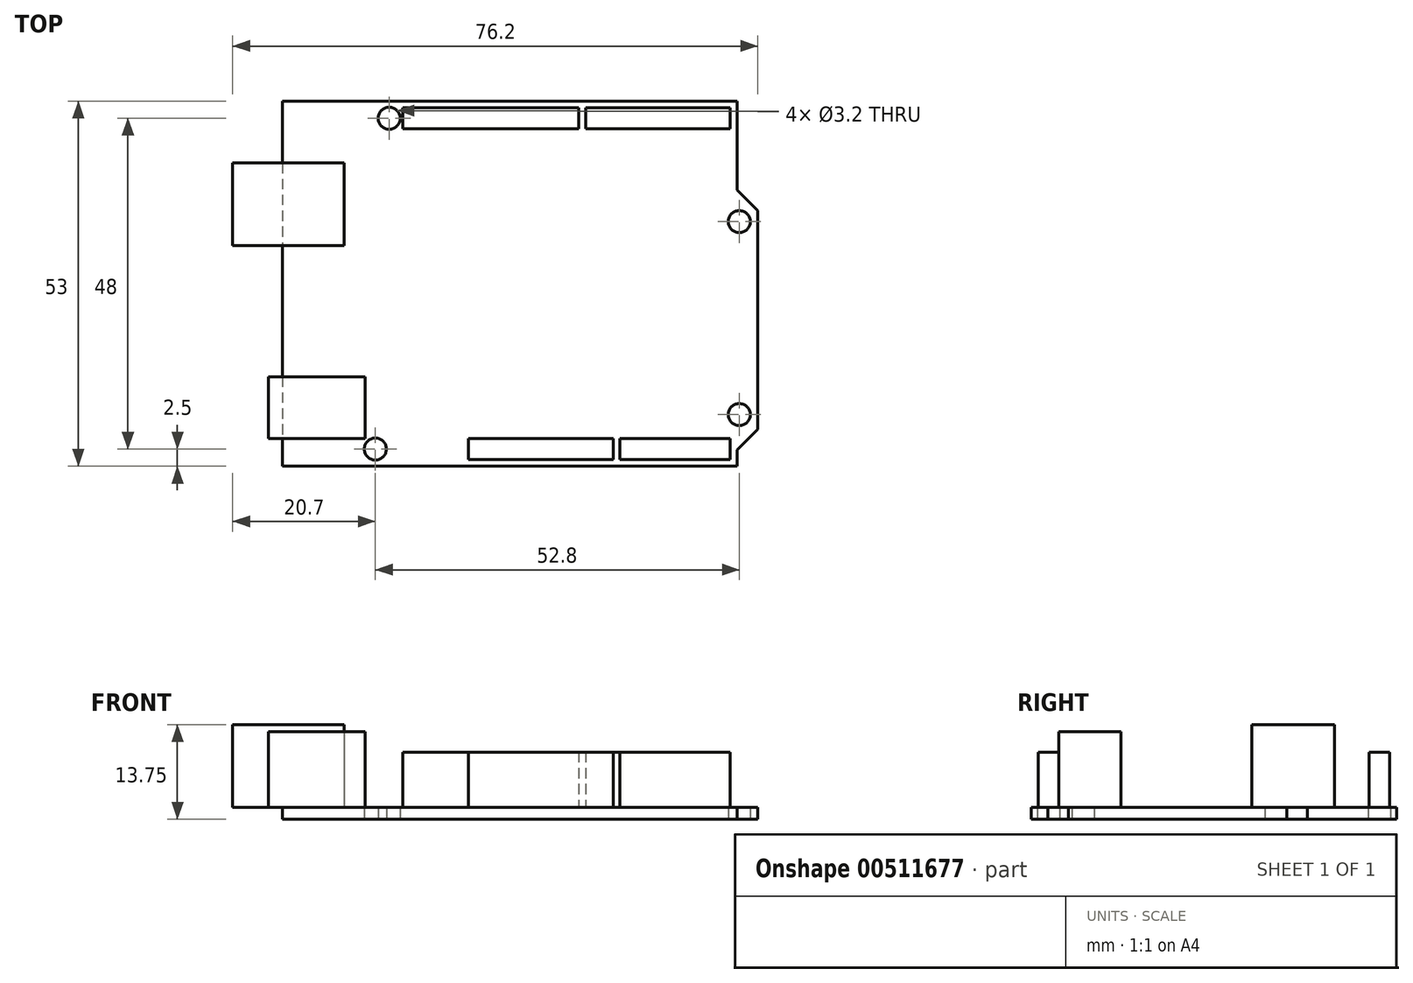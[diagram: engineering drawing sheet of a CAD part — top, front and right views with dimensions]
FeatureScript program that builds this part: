
annotation { "Feature Type Name" : "Feature", "Feature Type Description" : "" }
export const myFeature = defineFeature(function(context is Context, id is Id, definition is map)
    precondition{}
    {
        {
            var Q0;
            Q0=qCreatedBy(makeId("Top.planeOp"),FACE);
            var sketch = newSketch(context, id + "F0", { "sketchPlane" : qUnion([Q0])});
            skLineSegment(sketch, "E0.bottom", {"start": v(-36.44, 36.99) * mm, "end": v(32.56, 36.99) * mm});
            skLineSegment(sketch, "E0.top", {"start": v(-36.44, -16.01) * mm, "end": v(32.56, -16.01) * mm});
            skLineSegment(sketch, "E0.left", {"start": v(-36.44, 36.99) * mm, "end": v(-36.44, -16.01) * mm});
            skLineSegment(sketch, "E0.right", {"start": v(32.56, 36.99) * mm, "end": v(32.56, -16.01) * mm});
            skCircle(sketch, "E1", {"center": v(-22.94, -13.51) * mm, "radius": 1.6 * mm});
            skCircle(sketch, "E2", {"center": v(-20.94, 34.49) * mm, "radius": 1.6 * mm});
            skCircle(sketch, "E3", {"center": v(29.86, 19.49) * mm, "radius": 1.6 * mm});
            skCircle(sketch, "E4", {"center": v(29.86, -8.51) * mm, "radius": 1.6 * mm});
            skLineSegment(sketch, "E5", {"start": v(29.56, -16.01) * mm, "end": v(29.56, -13.64) * mm});
            skLineSegment(sketch, "E6", {"start": v(29.56, -13.64) * mm, "end": v(32.56, -10.64) * mm});
            skLineSegment(sketch, "E7", {"start": v(29.56, 36.99) * mm, "end": v(29.56, 24.07) * mm});
            skLineSegment(sketch, "E8", {"start": v(29.56, 24.07) * mm, "end": v(32.56, 21.07) * mm});
            skSolve(sketch);
        }
        {
            var Q0;
            {var subQ1=sQuery(id+"F0.wireOp",EDGE,"E0.left");Q0=makeQuery(id+"F0.imprint","IMPRINT",FACE,{"disambiguationData":[TD([[makeQuery(id+"F0.imprint","IMPRINT",EDGE,{"derivedFrom":subQ1}),1.0]])]});}
            extrude(context, id + "F1", {"entities" : qUnion([Q0]), "depth" : 1.75 * mm});
        }
        {
            var Q0;
            Q0=makeQuery(id+"F1.opExtrude","CAP_FACE",FACE,{"disambiguationData":[OSD([sQuery(id+"F0.wireOp",EDGE,"E0.bottom"),sQuery(id+"F0.wireOp",EDGE,"E0.top"),sQuery(id+"F0.wireOp",EDGE,"E0.left"),sQuery(id+"F0.wireOp",EDGE,"E0.right"),sQuery(id+"F0.wireOp",EDGE,"E1"),sQuery(id+"F0.wireOp",EDGE,"E2"),sQuery(id+"F0.wireOp",EDGE,"E3"),sQuery(id+"F0.wireOp",EDGE,"E4"),sQuery(id+"F0.wireOp",EDGE,"E5"),sQuery(id+"F0.wireOp",EDGE,"E6"),sQuery(id+"F0.wireOp",EDGE,"E7"),sQuery(id+"F0.wireOp",EDGE,"E8")])],"isStart":false});
            var sketch = newSketch(context, id + "F2", { "sketchPlane" : qUnion([Q0])});
            skLineSegment(sketch, "E9.bottom", {"start": v(-43.64, 27.99) * mm, "end": v(-27.44, 27.99) * mm});
            skLineSegment(sketch, "E9.top", {"start": v(-43.64, 15.99) * mm, "end": v(-27.44, 15.99) * mm});
            skLineSegment(sketch, "E9.left", {"start": v(-43.64, 27.99) * mm, "end": v(-43.64, 15.99) * mm});
            skLineSegment(sketch, "E9.right", {"start": v(-27.44, 27.99) * mm, "end": v(-27.44, 15.99) * mm});
            skSolve(sketch);
        }
        {
            var Q0;
            {var subQ0=sQuery(id+"F2.wireOp",EDGE,"E9.left");Q0=makeQuery(id+"F2.imprint","IMPRINT",FACE,{"disambiguationData":[TD([[makeQuery(id+"F2.imprint","IMPRINT",EDGE,{"derivedFrom":subQ0}),1.0]])]});}
            var Q1;
            {var subQ0=sQuery(id+"F2.wireOp",EDGE,"E9.right");Q1=makeQuery(id+"F2.imprint","IMPRINT",FACE,{"disambiguationData":[TD([[makeQuery(id+"F2.imprint","IMPRINT",EDGE,{"derivedFrom":subQ0}),-1.0]])]});}
            extrude(context, id + "F3", {"entities" : qUnion([Q0, Q1]), "operationType" : NewBodyOperationType.ADD, "depth" : 12 * mm});
        }
        {
            var Q0;
            Q0=makeQuery(id+"F1.opExtrude","CAP_FACE",FACE,{"disambiguationData":[OSD([sQuery(id+"F0.wireOp",EDGE,"E0.bottom"),sQuery(id+"F0.wireOp",EDGE,"E0.top"),sQuery(id+"F0.wireOp",EDGE,"E0.left"),sQuery(id+"F0.wireOp",EDGE,"E0.right"),sQuery(id+"F0.wireOp",EDGE,"E1"),sQuery(id+"F0.wireOp",EDGE,"E2"),sQuery(id+"F0.wireOp",EDGE,"E3"),sQuery(id+"F0.wireOp",EDGE,"E4"),sQuery(id+"F0.wireOp",EDGE,"E5"),sQuery(id+"F0.wireOp",EDGE,"E6"),sQuery(id+"F0.wireOp",EDGE,"E7"),sQuery(id+"F0.wireOp",EDGE,"E8")])],"isStart":false});
            var sketch = newSketch(context, id + "F4", { "sketchPlane" : qUnion([Q0])});
            skLineSegment(sketch, "E10.bottom", {"start": v(-38.44, -3.01) * mm, "end": v(-24.44, -3.01) * mm});
            skLineSegment(sketch, "E10.top", {"start": v(-38.44, -12.01) * mm, "end": v(-24.44, -12.01) * mm});
            skLineSegment(sketch, "E10.left", {"start": v(-38.44, -3.01) * mm, "end": v(-38.44, -12.01) * mm});
            skLineSegment(sketch, "E10.right", {"start": v(-24.44, -3.01) * mm, "end": v(-24.44, -12.01) * mm});
            skSolve(sketch);
        }
        {
            var Q0;
            {var subQ0=sQuery(id+"F4.wireOp",EDGE,"E10.right");Q0=makeQuery(id+"F4.imprint","IMPRINT",FACE,{"disambiguationData":[TD([[makeQuery(id+"F4.imprint","IMPRINT",EDGE,{"derivedFrom":subQ0}),-1.0]])]});}
            var Q1;
            {var subQ0=sQuery(id+"F4.wireOp",EDGE,"E10.left");Q1=makeQuery(id+"F4.imprint","IMPRINT",FACE,{"disambiguationData":[TD([[makeQuery(id+"F4.imprint","IMPRINT",EDGE,{"derivedFrom":subQ0}),1.0]])]});}
            extrude(context, id + "F5", {"entities" : qUnion([Q0, Q1]), "operationType" : NewBodyOperationType.ADD, "depth" : 11 * mm});
        }
        {
            var Q0;
            Q0=makeQuery(id+"F1.opExtrude","CAP_FACE",FACE,{"disambiguationData":[OSD([sQuery(id+"F0.wireOp",EDGE,"E0.bottom"),sQuery(id+"F0.wireOp",EDGE,"E0.top"),sQuery(id+"F0.wireOp",EDGE,"E0.left"),sQuery(id+"F0.wireOp",EDGE,"E0.right"),sQuery(id+"F0.wireOp",EDGE,"E1"),sQuery(id+"F0.wireOp",EDGE,"E2"),sQuery(id+"F0.wireOp",EDGE,"E3"),sQuery(id+"F0.wireOp",EDGE,"E4"),sQuery(id+"F0.wireOp",EDGE,"E5"),sQuery(id+"F0.wireOp",EDGE,"E6"),sQuery(id+"F0.wireOp",EDGE,"E7"),sQuery(id+"F0.wireOp",EDGE,"E8")])],"isStart":false});
            var sketch = newSketch(context, id + "F6", { "sketchPlane" : qUnion([Q0])});
            skLineSegment(sketch, "E11.bottom", {"start": v(-9.44, -12.01) * mm, "end": v(11.56, -12.01) * mm});
            skLineSegment(sketch, "E11.top", {"start": v(-9.44, -15.01) * mm, "end": v(11.56, -15.01) * mm});
            skLineSegment(sketch, "E11.left", {"start": v(-9.44, -12.01) * mm, "end": v(-9.44, -15.01) * mm});
            skLineSegment(sketch, "E11.right", {"start": v(11.56, -12.01) * mm, "end": v(11.56, -15.01) * mm});
            skLineSegment(sketch, "E12.bottom", {"start": v(12.56, -12.01) * mm, "end": v(28.56, -12.01) * mm});
            skLineSegment(sketch, "E12.top", {"start": v(12.56, -15.01) * mm, "end": v(28.56, -15.01) * mm});
            skLineSegment(sketch, "E12.left", {"start": v(12.56, -12.01) * mm, "end": v(12.56, -15.01) * mm});
            skLineSegment(sketch, "E12.right", {"start": v(28.56, -12.01) * mm, "end": v(28.56, -15.01) * mm});
            skLineSegment(sketch, "E13.bottom", {"start": v(-18.94, 35.99) * mm, "end": v(6.56, 35.99) * mm});
            skLineSegment(sketch, "E13.top", {"start": v(-18.94, 32.99) * mm, "end": v(6.56, 32.99) * mm});
            skLineSegment(sketch, "E13.left", {"start": v(-18.94, 35.99) * mm, "end": v(-18.94, 32.99) * mm});
            skLineSegment(sketch, "E13.right", {"start": v(6.56, 35.99) * mm, "end": v(6.56, 32.99) * mm});
            skLineSegment(sketch, "E14.bottom", {"start": v(7.56, 35.99) * mm, "end": v(28.56, 35.99) * mm});
            skLineSegment(sketch, "E14.top", {"start": v(7.56, 32.99) * mm, "end": v(28.56, 32.99) * mm});
            skLineSegment(sketch, "E14.left", {"start": v(7.56, 35.99) * mm, "end": v(7.56, 32.99) * mm});
            skLineSegment(sketch, "E14.right", {"start": v(28.56, 35.99) * mm, "end": v(28.56, 32.99) * mm});
            skSolve(sketch);
        }
        {
            var Q0;
            Q0=makeQuery(id+"F6.imprint","IMPRINT",FACE,{"disambiguationData":[TD([[makeQuery(id+"F6.imprint","IMPRINT",EDGE,{"derivedFrom":sQuery(id+"F6.wireOp",EDGE,"E11.bottom")}),-1.0]])]});
            var Q1;
            Q1=makeQuery(id+"F6.imprint","IMPRINT",FACE,{"disambiguationData":[TD([[makeQuery(id+"F6.imprint","IMPRINT",EDGE,{"derivedFrom":sQuery(id+"F6.wireOp",EDGE,"E12.bottom")}),-1.0]])]});
            var Q2;
            Q2=makeQuery(id+"F6.imprint","IMPRINT",FACE,{"disambiguationData":[TD([[makeQuery(id+"F6.imprint","IMPRINT",EDGE,{"derivedFrom":sQuery(id+"F6.wireOp",EDGE,"E14.bottom")}),-1.0]])]});
            var Q3;
            Q3=makeQuery(id+"F6.imprint","IMPRINT",FACE,{"disambiguationData":[TD([[makeQuery(id+"F6.imprint","IMPRINT",EDGE,{"derivedFrom":sQuery(id+"F6.wireOp",EDGE,"E13.bottom")}),-1.0]])]});
            extrude(context, id + "F7", {"entities" : qUnion([Q0, Q1, Q2, Q3]), "operationType" : NewBodyOperationType.ADD, "depth" : 8 * mm});
        }
    });
